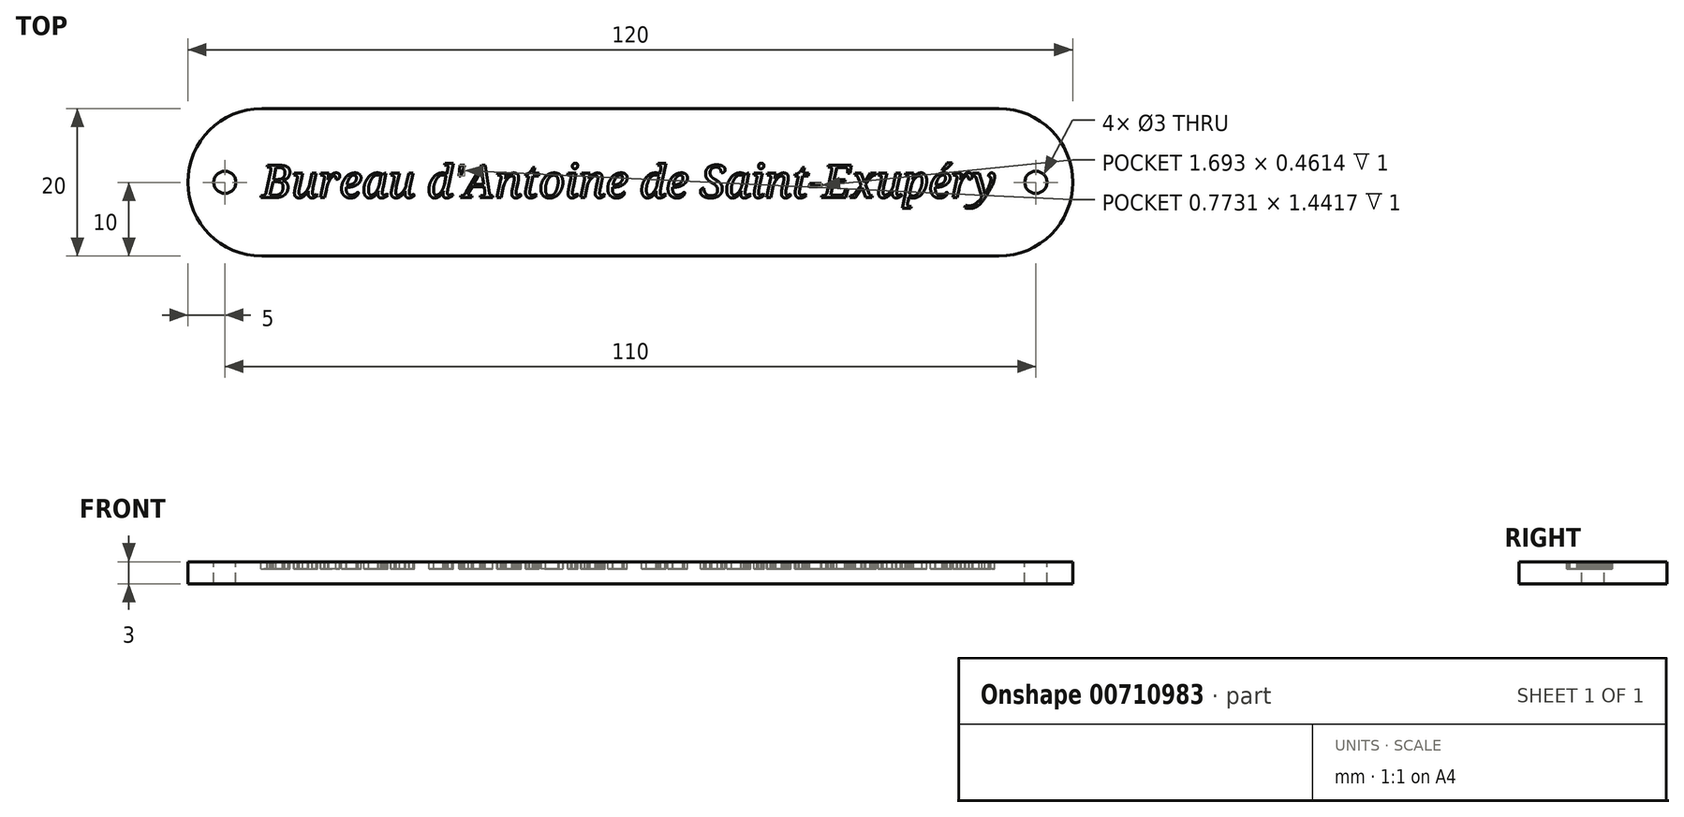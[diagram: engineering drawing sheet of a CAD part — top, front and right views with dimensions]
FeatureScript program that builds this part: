
annotation { "Feature Type Name" : "Feature", "Feature Type Description" : "" }
export const myFeature = defineFeature(function(context is Context, id is Id, definition is map)
    precondition{}
    {
        {
            var Q0;
            Q0=qCreatedBy(makeId("Top.planeOp"),FACE);
            var sketch = newSketch(context, id + "F0", { "sketchPlane" : qUnion([Q0])});
            skLineSegment(sketch, "E0.bottom", {"start": v(-50, 10) * mm, "end": v(50, 10) * mm});
            skLineSegment(sketch, "E0.top", {"start": v(-50, -10) * mm, "end": v(50, -10) * mm});
            skArc(sketch, "E1", {"start": v(-50, 10) * mm, "mid": v(-60, 0) * mm, "end": v(-50, -10) * mm});
            skArc(sketch, "E2", {"start": v(50, -10) * mm, "mid": v(60, 0) * mm, "end": v(50, 10) * mm});
            skSolve(sketch);
        }
        {
            var Q0;
            Q0=makeQuery(id+"F0.imprint","IMPRINT",FACE,{"disambiguationData":[TD([[makeQuery(id+"F0.imprint","IMPRINT",EDGE,{"derivedFrom":sQuery(id+"F0.wireOp",EDGE,"E0.bottom")}),-1.0]])]});
            extrude(context, id + "F1", {"entities" : qUnion([Q0]), "depth" : 3 * mm, "offsetDistance" : 25 * mm});
        }
        {
            var Q0;
            Q0=makeQuery(id+"F1.opExtrude","CAP_FACE",FACE,{"disambiguationData":[OSD([sQuery(id+"F0.wireOp",EDGE,"E0.bottom"),sQuery(id+"F0.wireOp",EDGE,"E0.top"),sQuery(id+"F0.wireOp",EDGE,"E1"),sQuery(id+"F0.wireOp",EDGE,"E2")])],"isStart":false});
            var sketch = newSketch(context, id + "F2", { "sketchPlane" : qUnion([Q0])});
            skText(sketch, "E3", { "text": "Bureau d\'Antoine de Saint-Exupéry", "fontName": "NotoSerif-Italic.ttf"});
            skPoint(sketch, "E4.positionSnap0", {"position": v(-49.32, 0) * mm});
            skPoint(sketch, "E5", {"position": v(-55, 0) * mm});
            skPoint(sketch, "E6", {"position": v(55, 0) * mm});
            const initialGuessF2  = {"E3": [-0.05, -0.00207, 1, 0, 0.00442]};
            skSetInitialGuess(sketch, initialGuessF2);
            skSolve(sketch);
        }
        {
            var Q0;
            Q0 = qSketchRegion(id + "F2", true);
            extrude(context, id + "F3", {"entities" : qUnion([Q0]), "operationType" : NewBodyOperationType.REMOVE, "oppositeDirection" : true, "depth" : 1 * mm, "offsetDistance" : 25 * mm});
        }
        {
            var Q0;
            Q0=sQuery(id+"F2.wireOp",VERTEX,"E5");
            var Q1;
            Q1=sQuery(id+"F2.wireOp",VERTEX,"E6");
            var Q2;
            Q2=makeQuery(id+"F1.opExtrude","SWEPT_BODY",BODY,{"disambiguationData":[OSD([sQuery(id+"F0.wireOp",EDGE,"E0.bottom"),sQuery(id+"F0.wireOp",EDGE,"E0.top"),sQuery(id+"F0.wireOp",EDGE,"E1"),sQuery(id+"F0.wireOp",EDGE,"E2")])]});
            hole(context, id + "F4", {"style" : HoleStyle.SIMPLE, "endStyle" : HoleEndStyle.THROUGH, "holeDiameter" : 3 * mm, "majorDiameter" : 5 * mm, "isTappedThrough" : true, "tappedDepth" : 12 * mm, "tapClearance" : 3, "locations" : qUnion([Q0, Q1]), "scope" : qUnion([Q2])});
        }
        {
            var Q0;
            Q0 = qSketchRegion(id + "F0", true);
            extrude(context, id + "F5", {"entities" : qUnion([Q0]), "depth" : 3 * mm, "offsetDistance" : 25 * mm});
        }
        {
            var Q0;
            Q0=sQuery(id+"F2.wireOp",VERTEX,"E5");
            var Q1;
            Q1=sQuery(id+"F2.wireOp",VERTEX,"E6");
            var Q2;
            Q2=makeQuery(id+"F5.opExtrude","SWEPT_BODY",BODY,{"disambiguationData":[OSD([sQuery(id+"F0.wireOp",EDGE,"E0.bottom"),sQuery(id+"F0.wireOp",EDGE,"E0.top"),sQuery(id+"F0.wireOp",EDGE,"E1"),sQuery(id+"F0.wireOp",EDGE,"E2")])]});
            hole(context, id + "F6", {"style" : HoleStyle.SIMPLE, "endStyle" : HoleEndStyle.THROUGH, "holeDiameter" : 3 * mm, "majorDiameter" : 5 * mm, "isTappedThrough" : true, "tappedDepth" : 12 * mm, "tapClearance" : 3, "locations" : qUnion([Q0, Q1]), "scope" : qUnion([Q2])});
        }
    });
